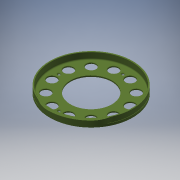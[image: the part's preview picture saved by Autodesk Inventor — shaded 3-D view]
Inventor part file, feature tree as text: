
AUTODESK INVENTOR PART (.ipt)
format: ipt  version: 2018 (Build 220112000, 112)  size: 273,408 bytes
history: native  units: mm
features: sketch x3, extrude x3, hole x2, chamfer x2, pattern_circular x2, fillet x2, revolve x1, other x1, projected_geometry x1
ambient origin geometry x8: Origin, YZ Plane, XZ Plane, XY Plane, X Axis, Y Axis, Z Axis, Center Point
bodies: Solid1 (feature_tree)
feature tree (17):
  sketch  "Sketch1"  dims[d0=35.0mm d1=68.0mm]
  extrude  "Extrusion1"  Depth=35.0mm
  extrude  "Extrusion2"  Depth=72.0mm
  extrude  "Extrusion3"  Depth=0.2mm
  revolve  "Revolution1"  [1 undecoded]
  sketch  "Sketch3"  dims[d4=32.36mm d5=1.06mm d6=5.14mm d7=26.16mm d8=10.3mm d9=1.54mm d10=16.74mm d11=26.16mm d12=37.0mm d13=33.97mm d14=33.07mm d15=13.335mm d16=20.0mm d17=19.0mm d18=37.0mm d19=19.0mm d20=20.0mm d21=20.0mm d22=6.5mm d23=0.0mm d24=5.5mm d25=0.0mm d26=2.5mm d27=0.0mm d28=0.5mm d29=2.0mm d30=0.25mm d31=90.0deg d32=54.0mm d33=27.0mm d35=6.99mm d36=8.0mm d37=6.0mm d38=4.0mm d39=2.0mm d40=90.0deg d41=27.0mm d42=0.0mm d43=2.0mm d44=6.0mm d45=4.0mm d46=2.0mm d47=90.0deg d48=27.0mm d49=0.0mm d50=0.5mm d51=2.0mm d52=45.0deg d53=0.2mm d54=2.0mm d55=45.0deg d56=120.0mm d57=360.0deg d59=30.0mm d60=180.0deg d62=1.0mm d63=0.2mm]
  hole  "Hole1"  [1 undecoded]
  hole  "Hole2"  [1 undecoded]
  chamfer  "Chamfer1"  Distance=1.54mm
  chamfer  "Chamfer2"  Distance=16.74mm
  other  "Work Axis1"
  pattern_circular  "Circular Pattern1"  [2 undecoded]
  pattern_circular  "Circular Pattern2"  [2 undecoded]
  fillet  "Fillet1"  Radius=33.97mm
  fillet  "Fillet2"  Radius=33.07mm
  sketch  "Sketch2"  dims[d2=70.0mm d3=72.0mm]
  projected_geometry  "Project Cut Edges1"
note: 7 required parameter values undecoded (feature->parameter linkage not recoverable at this tier; creation-order binding heuristic only, values carry confidence <= 0.55)